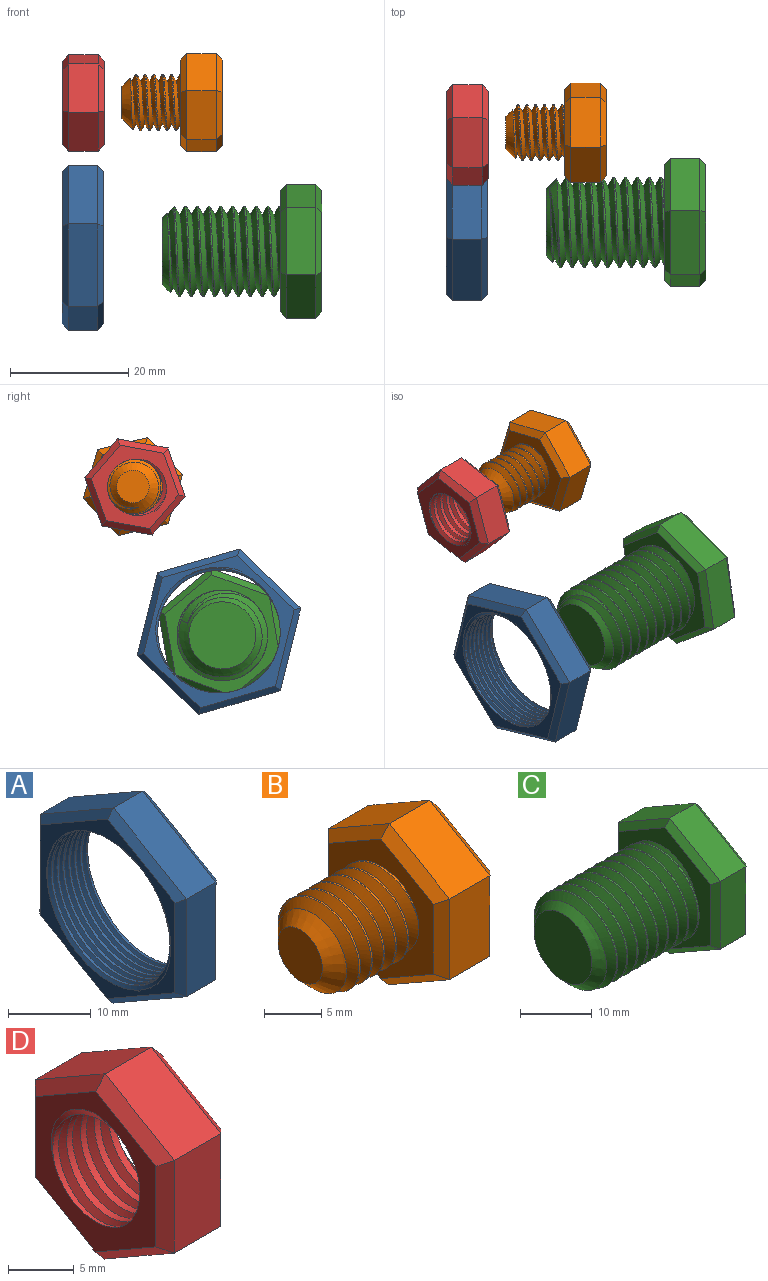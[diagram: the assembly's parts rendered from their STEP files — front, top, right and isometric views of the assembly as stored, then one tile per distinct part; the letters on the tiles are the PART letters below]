
ASSEMBLY  parts=4 mates=2
PART A: 23 faces, bbox 8.8x25.6x29.2 mm
  f0: cylinder r=10.38mm len=20.76mm, axis (1,0,0), area 164.5mm2, adj f7,f8,f21,f22
  f1: plane 12.48x7.25mm, normal (0,-0.5,0.86), area 72.2mm2, adj f2,f6,f14,f18
  f2: plane 14.43x5mm, normal (0,-1,0), area 72.2mm2, adj f1,f3,f12,f16
  f3: plane 12.52x7.19mm, normal (0,-0.5,-0.87), area 72.2mm2, adj f2,f4,f10,f15
  f4: plane 12.48x7.25mm, normal (0,0.5,-0.86), area 72.2mm2, adj f3,f5,f9,f17
  f5: plane 14.43x5mm, normal (0,1,0), area 72.2mm2, adj f4,f6,f11,f19
  f6: plane 12.52x7.19mm, normal (0,0.5,0.87), area 72.2mm2, adj f1,f5,f13,f20
  f7: plane 26.89x23.36mm, normal (-1,0,0), area 107.6mm2, adj f0,f9,f10,f11,f12,f13,f14,f21
  f8: plane 26.89x23.36mm, normal (1,0,0), area 107.6mm2, adj f0,f15,f16,f17,f18,f19,f20,f21
  f9: plane 12.48x7.82mm, normal (-0.71,0.36,-0.61), area 19.6mm2, adj f4,f7,f10,f11
  f10: plane 12.52x7.77mm, normal (-0.71,-0.35,-0.61), area 19.6mm2, adj f3,f7,f9,f12
  f11: plane 14.43x1.04mm, normal (-0.71,0.71,0), area 19.6mm2, adj f5,f7,f9,f13
  f12: plane 14.43x1.04mm, normal (-0.71,-0.71,0), area 19.6mm2, adj f2,f7,f10,f14
  f13: plane 12.52x7.77mm, normal (-0.71,0.35,0.61), area 19.6mm2, adj f6,f7,f11,f14
  f14: plane 12.48x7.82mm, normal (-0.71,-0.36,0.61), area 19.6mm2, adj f1,f7,f12,f13
  f15: plane 12.52x7.77mm, normal (0.71,-0.35,-0.61), area 19.6mm2, adj f3,f8,f16,f17
  f16: plane 14.43x1.04mm, normal (0.71,-0.71,0), area 19.6mm2, adj f2,f8,f15,f18
  f17: plane 12.48x7.82mm, normal (0.71,0.36,-0.61), area 19.6mm2, adj f4,f8,f15,f19
  f18: plane 12.48x7.82mm, normal (0.71,-0.36,0.61), area 19.6mm2, adj f1,f8,f16,f20
  f19: plane 14.43x1.04mm, normal (0.71,0.71,0), area 19.6mm2, adj f5,f8,f17,f20
  f20: plane 12.52x7.77mm, normal (0.71,0.35,0.61), area 19.6mm2, adj f6,f8,f18,f19
  f21: bspline ~25.27x21.88mm, area 304.2mm2, adj f0,f7,f8,f22
  f22: bspline ~25.27x21.88mm, area 71.5mm2, adj f0,f7,f8,f21
PART B: 25 faces, bbox 17.8x15.9x18.1 mm
  f0: cylinder r=4.75mm len=9.5mm, axis (1,0,0), area 28.1mm2, adj f1,f2,f4,f12
  f1: bspline ~10.97x9.91mm, area 196.7mm2, adj f0,f2,f4,f12
  f2: bspline ~10.97x10.66mm, area 196.6mm2, adj f0,f1,f4,f12
  f3: plane 5.5x5.5mm, normal (-1,0,0), area 23.8mm2, adj f4
  f4: cone r=4.75mm half-angle=45deg, axis (1,0,0), area 47.4mm2, adj f0,f1,f2,f3
  f5: plane 7.48x5mm, normal (0,-0.5,0.86), area 43.3mm2, adj f6,f10,f18,f22
  f6: plane 8.66x5mm, normal (0,-1,0), area 43.3mm2, adj f5,f7,f16,f20
  f7: plane 7.52x5mm, normal (0,-0.5,-0.87), area 43.3mm2, adj f6,f8,f14,f19
  f8: plane 7.48x5mm, normal (0,0.5,-0.86), area 43.3mm2, adj f7,f9,f13,f21
  f9: plane 8.66x5mm, normal (0,1,0), area 43.3mm2, adj f8,f10,f15,f23
  f10: plane 7.52x5mm, normal (0,0.5,0.87), area 43.3mm2, adj f5,f9,f17,f24
  f11: plane 15.01x13.03mm, normal (1,0,0), area 146.4mm2, adj f13,f14,f15,f16,f17,f18
  f12: plane 15.83x13.85mm, normal (-1,0,0), area 89.2mm2, adj f0,f1,f2,f19,f20,f21,f22,f23
  f13: plane 7.49x4.93mm, normal (0.71,0.36,-0.61), area 11.4mm2, adj f8,f11,f14,f15
  f14: plane 7.52x4.88mm, normal (0.71,-0.35,-0.61), area 11.4mm2, adj f7,f11,f13,f16
  f15: plane 8.66x1.03mm, normal (0.71,0.71,0), area 11.4mm2, adj f9,f11,f13,f17
  f16: plane 8.66x1.03mm, normal (0.71,-0.71,0), area 11.4mm2, adj f6,f11,f14,f18
  f17: plane 7.52x4.88mm, normal (0.71,0.35,0.61), area 11.4mm2, adj f10,f11,f15,f18
  f18: plane 7.49x4.93mm, normal (0.71,-0.36,0.61), area 11.4mm2, adj f5,f11,f16,f17
  f19: plane 7.52x4.88mm, normal (-0.71,-0.35,-0.61), area 11.4mm2, adj f7,f12,f20,f21
  f20: plane 8.66x1.03mm, normal (-0.71,-0.71,0), area 11.4mm2, adj f6,f12,f19,f22
  f21: plane 7.49x4.93mm, normal (-0.71,0.36,-0.61), area 11.4mm2, adj f8,f12,f19,f23
  f22: plane 7.49x4.93mm, normal (-0.71,-0.36,0.61), area 11.4mm2, adj f5,f12,f20,f24
  f23: plane 8.66x1.03mm, normal (-0.71,0.71,0), area 11.4mm2, adj f9,f12,f21,f24
  f24: plane 7.52x4.88mm, normal (-0.71,0.35,0.61), area 11.4mm2, adj f10,f12,f22,f23
PART C: 26 faces, bbox 27.7x20x23.1 mm
  f0: cylinder r=7.68mm len=18mm, axis (1,0,0), area 139.1mm2, adj f1,f2,f5,f13
  f1: bspline ~20.88x17.74mm, area 713.8mm2, adj f0,f2,f4,f5,f13
  f2: bspline ~21.88x17.74mm, area 715.1mm2, adj f0,f1,f4,f5,f13
  f3: plane 11.36x11.36mm, normal (-1,0,0), area 101.4mm2, adj f4
  f4: cone r=7.68mm half-angle=45deg, axis (1,0,0), area 63.2mm2, adj f1,f2,f3,f5
  f5: cone r=7.68mm half-angle=45deg, axis (1,0,0), area 13.2mm2, adj f0,f1,f2,f4
  f6: plane 9.98x5.81mm, normal (0,-0.5,0.86), area 57.7mm2, adj f7,f11,f19,f23
  f7: plane 11.55x5mm, normal (0,-1,0), area 57.7mm2, adj f6,f8,f17,f21
  f8: plane 10.02x5.74mm, normal (0,-0.5,-0.87), area 57.7mm2, adj f7,f9,f15,f20
  f9: plane 9.98x5.81mm, normal (0,0.5,-0.86), area 57.7mm2, adj f8,f10,f14,f22
  f10: plane 11.55x5mm, normal (0,1,0), area 57.7mm2, adj f9,f11,f16,f24
  f11: plane 10.02x5.74mm, normal (0,0.5,0.87), area 57.7mm2, adj f6,f10,f18,f25
  f12: plane 20.78x18.04mm, normal (1,0,0), area 280.6mm2, adj f14,f15,f16,f17,f18,f19
  f13: plane 20.78x18.04mm, normal (-1,0,0), area 125.2mm2, adj f0,f1,f2,f20,f21,f22,f23,f24
  f14: plane 9.98x6.38mm, normal (0.71,0.36,-0.61), area 15.5mm2, adj f9,f12,f15,f16
  f15: plane 10.02x6.32mm, normal (0.71,-0.35,-0.61), area 15.5mm2, adj f8,f12,f14,f17
  f16: plane 11.55x1.04mm, normal (0.71,0.71,0), area 15.5mm2, adj f10,f12,f14,f18
  f17: plane 11.55x1.04mm, normal (0.71,-0.71,0), area 15.5mm2, adj f7,f12,f15,f19
  f18: plane 10.02x6.32mm, normal (0.71,0.35,0.61), area 15.5mm2, adj f11,f12,f16,f19
  f19: plane 9.98x6.38mm, normal (0.71,-0.36,0.61), area 15.5mm2, adj f6,f12,f17,f18
  f20: plane 10.02x6.32mm, normal (-0.71,-0.35,-0.61), area 15.5mm2, adj f8,f13,f21,f22
  f21: plane 11.55x1.04mm, normal (-0.71,-0.71,0), area 15.5mm2, adj f7,f13,f20,f23
  f22: plane 9.98x6.38mm, normal (-0.71,0.36,-0.61), area 15.5mm2, adj f9,f13,f20,f24
  f23: plane 9.98x6.38mm, normal (-0.71,-0.36,0.61), area 15.5mm2, adj f6,f13,f21,f25
  f24: plane 11.55x1.04mm, normal (-0.71,0.71,0), area 15.5mm2, adj f10,f13,f22,f25
  f25: plane 10.02x6.32mm, normal (-0.71,0.35,0.61), area 15.5mm2, adj f11,f13,f23,f24
PART D: 23 faces, bbox 9.1x15.4x17.7 mm
  f0: plane 7.49x5mm, normal (0,-0.5,0.86), area 43.3mm2, adj f1,f5,f13,f17
  f1: plane 8.66x5mm, normal (0,-1,0), area 43.3mm2, adj f0,f2,f11,f15
  f2: plane 7.51x5mm, normal (0,-0.5,-0.87), area 43.3mm2, adj f1,f3,f9,f14
  f3: plane 7.49x5mm, normal (0,0.5,-0.86), area 43.3mm2, adj f2,f4,f8,f16
  f4: plane 8.66x5mm, normal (0,1,0), area 43.3mm2, adj f3,f5,f10,f18
  f5: plane 7.51x5mm, normal (0,0.5,0.87), area 43.3mm2, adj f0,f4,f12,f19
  f6: plane 15.37x13.38mm, normal (-1,0,0), area 71.4mm2, adj f8,f9,f10,f11,f12,f13,f20,f21
  f7: plane 15.37x13.38mm, normal (1,0,0), area 71.4mm2, adj f14,f15,f16,f17,f18,f19,f20,f21
  f8: plane 7.49x4.93mm, normal (-0.71,0.36,-0.61), area 11.4mm2, adj f3,f6,f9,f10
  f9: plane 7.51x4.89mm, normal (-0.71,-0.35,-0.61), area 11.4mm2, adj f2,f6,f8,f11
  f10: plane 8.66x1.02mm, normal (-0.71,0.71,0), area 11.4mm2, adj f4,f6,f8,f12
  f11: plane 8.66x1.02mm, normal (-0.71,-0.71,0), area 11.4mm2, adj f1,f6,f9,f13
  f12: plane 7.51x4.89mm, normal (-0.71,0.35,0.61), area 11.4mm2, adj f5,f6,f10,f13
  f13: plane 7.49x4.93mm, normal (-0.71,-0.36,0.61), area 11.4mm2, adj f0,f6,f11,f12
  f14: plane 7.51x4.89mm, normal (0.71,-0.35,-0.61), area 11.4mm2, adj f2,f7,f15,f16
  f15: plane 8.66x1.02mm, normal (0.71,-0.71,0), area 11.4mm2, adj f1,f7,f14,f17
  f16: plane 7.49x4.93mm, normal (0.71,0.36,-0.61), area 11.4mm2, adj f3,f7,f14,f18
  f17: plane 7.49x4.93mm, normal (0.71,-0.36,0.61), area 11.4mm2, adj f0,f7,f15,f19
  f18: plane 8.66x1.02mm, normal (0.71,0.71,0), area 11.4mm2, adj f4,f7,f16,f19
  f19: plane 7.51x4.89mm, normal (0.71,0.35,0.61), area 11.4mm2, adj f5,f7,f17,f18
  f20: cylinder r=4.66mm len=9.32mm, axis (1,0,0), area 85.4mm2, adj f6,f7,f21,f22
  f21: bspline ~12.5x10.82mm, area 128.4mm2, adj f6,f7,f20,f22
  f22: bspline ~12.5x10.82mm, area 128.5mm2, adj f6,f7,f20,f21
PLACE A rot(axis=(0,0.6,-0.8),180deg) t=(-55.27,-6.86,23.48)mm fixed
PLACE B rot(axis=(-1,0,0),43.8deg) t=(-31.66,7.73,48.08)mm
PLACE C rot(axis=(1,0,0),109.9deg) t=(-14.77,-7.43,22.87)mm
PLACE D rot(axis=(1,0,0),100.2deg) t=(-48.16,7.38,48.02)mm fixed
MATE cylindrical C.f0 <-> A.f7  axis (-1,0,0) through (-38.27,-7.43,22.87)mm
MATE cylindrical B.f0 <-> D.f6  axis (-1,0,0) through (-45.16,7.73,48.08)mm
